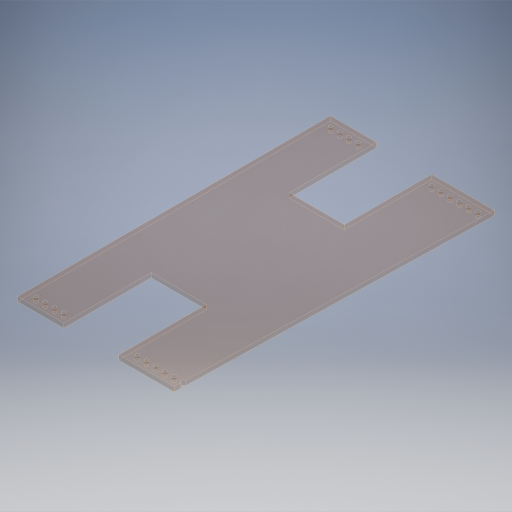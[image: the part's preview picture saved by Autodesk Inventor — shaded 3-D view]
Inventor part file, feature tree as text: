
AUTODESK INVENTOR PART (.ipt)
format: ipt  version: 2024.2 (Build 282272000, 272)  size: 371,712 bytes
history: native  units: in
note: dims shown in document units (in); Inventor stores cm internally (conversion verified against a paired STEP export)
features: extrude x3, sketch x2, projected_geometry x1
ambient origin geometry x8: Origin, YZ Plane, XZ Plane, XY Plane, X Axis, Y Axis, Z Axis, Center Point
bodies: Solid1 (feature_tree)
feature tree (6):
  extrude  "Extrusion1"  Depth=17.0in
  sketch  "Sketch2"  dims[d2=2.5in d3=4.75in d4=3.0in d5=2.5in d6=4.75in d7=3.0in d8=4.75in d9=4.75in d10=0.196in d11=0.5in d12=0.5in d13=1.5748in d15=0.5in d16=0.3937in d18=1.0in d20=0.196in d21=0.5in d22=0.5in d23=3.1496in d25=0.5in d26=0.3937in d28=1.0in d30=0.5in d31=0.25in d32=0.0in d33=8.5in d34=1.0in d35=0.0in d36=1.0in d37=0.0in]
  extrude  "Extrusion2"  Depth=4.75in
  extrude  "Extrusion3"  Depth=3.0in
  sketch  "Sketch1"  dims[d0=23.748in d1=17.0in]
  projected_geometry  "Projected Loop1"
